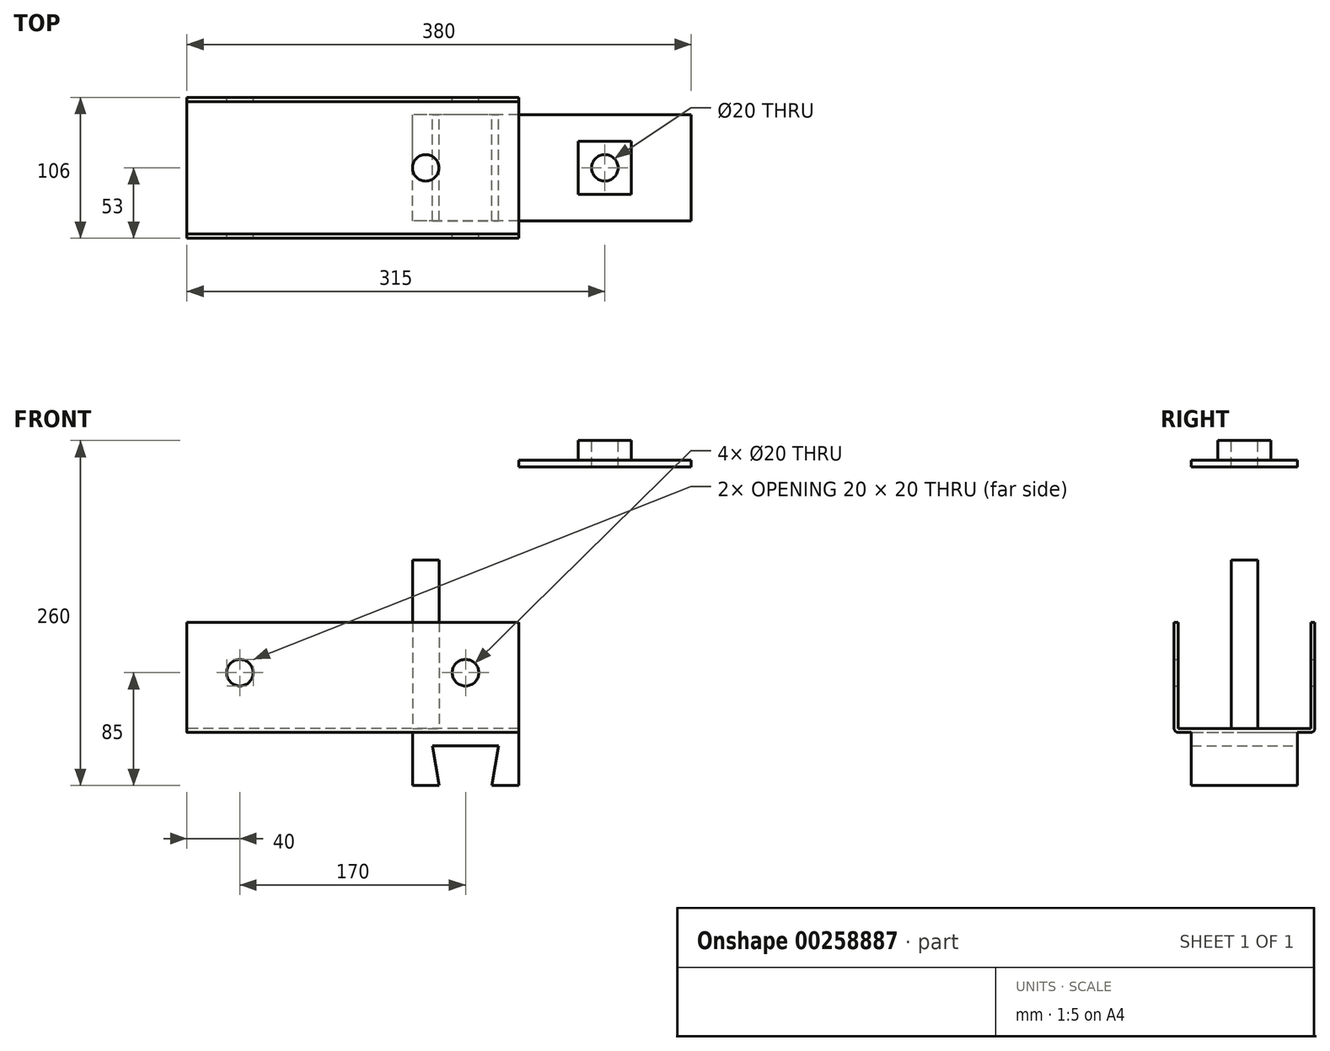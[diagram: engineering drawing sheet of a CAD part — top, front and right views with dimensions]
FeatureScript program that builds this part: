
annotation { "Feature Type Name" : "Feature", "Feature Type Description" : "" }
export const myFeature = defineFeature(function(context is Context, id is Id, definition is map)
    precondition{}
    {
        {
            var Q0;
            Q0=qCreatedBy(makeId("Front.planeOp"),FACE);
            var sketch = newSketch(context, id + "F0", { "sketchPlane" : qUnion([Q0])});
            skLineSegment(sketch, "E0", {"start": v(0, 0) * mm, "end": v(0, 5) * mm});
            skLineSegment(sketch, "E1", {"start": v(0, 5) * mm, "end": v(250, 5) * mm});
            skLineSegment(sketch, "E2", {"start": v(250, 5) * mm, "end": v(250, 0) * mm});
            skLineSegment(sketch, "E3", {"start": v(250, 0) * mm, "end": v(0, 0) * mm});
            skLineSegment(sketch, "E4", {"start": v(0, 5) * mm, "end": v(0, 85) * mm});
            skLineSegment(sketch, "E5", {"start": v(0, 85) * mm, "end": v(250, 85) * mm});
            skLineSegment(sketch, "E6", {"start": v(250, 85) * mm, "end": v(250, 5) * mm});
            skLineSegment(sketch, "E7", {"start": v(0, 45) * mm, "end": v(40, 45) * mm, "construction": true});
            skLineSegment(sketch, "E8", {"start": v(40, 45) * mm, "end": v(40, 85) * mm, "construction": true});
            skLineSegment(sketch, "E9", {"start": v(40, 5) * mm, "end": v(40, 45) * mm, "construction": true});
            skCircle(sketch, "E10", {"center": v(40, 45) * mm, "radius": 10 * mm});
            skLineSegment(sketch, "E11", {"start": v(210, 85) * mm, "end": v(210, 45) * mm, "construction": true});
            skLineSegment(sketch, "E12", {"start": v(210, 45) * mm, "end": v(250, 45) * mm, "construction": true});
            skLineSegment(sketch, "E13", {"start": v(210, 5) * mm, "end": v(210, 45) * mm, "construction": true});
            skCircle(sketch, "E14", {"center": v(210, 45) * mm, "radius": 10 * mm});
            skLineSegment(sketch, "E15", {"start": v(250, 0) * mm, "end": v(250, -40) * mm});
            skLineSegment(sketch, "E16", {"start": v(250, -40) * mm, "end": v(230, -40) * mm});
            skLineSegment(sketch, "E17", {"start": v(230, -40) * mm, "end": v(235, -10) * mm});
            skLineSegment(sketch, "E18", {"start": v(235, -10) * mm, "end": v(185, -10) * mm});
            skLineSegment(sketch, "E19", {"start": v(185, -10) * mm, "end": v(190, -40) * mm});
            skLineSegment(sketch, "E20", {"start": v(190, -40) * mm, "end": v(170, -40) * mm});
            skLineSegment(sketch, "E21", {"start": v(170, -40) * mm, "end": v(170, 0) * mm});
            skLineSegment(sketch, "E22", {"start": v(250, 200) * mm, "end": v(380, 200) * mm});
            skLineSegment(sketch, "E23", {"start": v(380, 200) * mm, "end": v(380, 205) * mm});
            skLineSegment(sketch, "E24", {"start": v(250, 205) * mm, "end": v(250, 200) * mm});
            skLineSegment(sketch, "E25", {"start": v(295, 205) * mm, "end": v(295, 220) * mm});
            skLineSegment(sketch, "E26", {"start": v(295, 220) * mm, "end": v(335, 220) * mm});
            skLineSegment(sketch, "E27", {"start": v(335, 220) * mm, "end": v(335, 205) * mm});
            skLineSegment(sketch, "E28", {"start": v(250, 205) * mm, "end": v(295, 205) * mm});
            skLineSegment(sketch, "E29", {"start": v(335, 205) * mm, "end": v(380, 205) * mm});
            skSolve(sketch);
        }
        {
            var Q0;
            Q0=qCreatedBy(makeId("Right.planeOp"),FACE);
            var sketch = newSketch(context, id + "F1", { "sketchPlane" : qUnion([Q0])});
            skLineSegment(sketch, "E30", {"start": v(0, 0) * mm, "end": v(50, 0) * mm});
            skLineSegment(sketch, "E31", {"start": v(53, 3) * mm, "end": v(53, 83) * mm});
            skLineSegment(sketch, "E32", {"start": v(53, 83) * mm, "end": v(50, 83) * mm});
            skLineSegment(sketch, "E33", {"start": v(50, 83) * mm, "end": v(50, 3) * mm});
            skLineSegment(sketch, "E34", {"start": v(50, 3) * mm, "end": v(-50, 3) * mm});
            skLineSegment(sketch, "E35", {"start": v(-50, 3) * mm, "end": v(-50, 83) * mm});
            skLineSegment(sketch, "E36", {"start": v(-50, 83) * mm, "end": v(-53, 83) * mm});
            skLineSegment(sketch, "E37", {"start": v(-53, 83) * mm, "end": v(-53, 3) * mm});
            skLineSegment(sketch, "E38", {"start": v(-50, 0) * mm, "end": v(0, 0) * mm});
            skPoint(sketch, "E39.visualSharp", {"position": v(-53, 0) * mm});
            skArc(sketch, "E39.filletArc", {"start": v(-53, 3) * mm, "mid": v(-52.12, 0.88) * mm, "end": v(-50, 0) * mm});
            skPoint(sketch, "E40.visualSharp", {"position": v(53, 0) * mm});
            skArc(sketch, "E40.filletArc", {"start": v(50, 0) * mm, "mid": v(52.12, 0.88) * mm, "end": v(53, 3) * mm});
            skLineSegment(sketch, "E41", {"start": v(-40, 0) * mm, "end": v(-40, -40) * mm});
            skLineSegment(sketch, "E42", {"start": v(-40, -40) * mm, "end": v(0, -40) * mm});
            skLineSegment(sketch, "E43", {"start": v(0, -40) * mm, "end": v(40, -40) * mm});
            skLineSegment(sketch, "E44", {"start": v(40, -40) * mm, "end": v(40, 0) * mm});
            skLineSegment(sketch, "E45", {"start": v(0, 200) * mm, "end": v(40, 200) * mm});
            skLineSegment(sketch, "E46", {"start": v(40, 200) * mm, "end": v(40, 205) * mm});
            skLineSegment(sketch, "E47", {"start": v(40, 205) * mm, "end": v(20, 205) * mm});
            skLineSegment(sketch, "E48", {"start": v(20, 205) * mm, "end": v(20, 220) * mm});
            skLineSegment(sketch, "E49", {"start": v(20, 220) * mm, "end": v(-20, 220) * mm});
            skLineSegment(sketch, "E50", {"start": v(-20, 220) * mm, "end": v(-20, 205) * mm});
            skLineSegment(sketch, "E51", {"start": v(-20, 205) * mm, "end": v(-40, 205) * mm});
            skLineSegment(sketch, "E52", {"start": v(-40, 205) * mm, "end": v(-40, 200) * mm});
            skLineSegment(sketch, "E53", {"start": v(-40, 200) * mm, "end": v(0, 200) * mm});
            skSolve(sketch);
        }
        {
            var Q0;
            Q0=qCreatedBy(makeId("Top.planeOp"),FACE);
            var sketch = newSketch(context, id + "F2", { "sketchPlane" : qUnion([Q0])});
            skCircle(sketch, "E54", {"center": v(180, 0) * mm, "radius": 10 * mm});
            skSolve(sketch);
        }
        {
            var Q0;
            Q0=makeQuery(id+"F0.imprint","IMPRINT",FACE,{"disambiguationData":[TD([[makeQuery(id+"F0.imprint","IMPRINT",EDGE,{"derivedFrom":sQuery(id+"F0.wireOp",EDGE,"E1")}),1.0]])]});
            var Q1;
            {var subQ3=sQuery(id+"F0.wireOp",EDGE,"E0");Q1=makeQuery(id+"F0.imprint","IMPRINT",FACE,{"disambiguationData":[TD([[makeQuery(id+"F0.imprint","IMPRINT",EDGE,{"derivedFrom":subQ3}),-1.0]])]});}
            var Q2;
            {var subQ0=sQuery(id+"F0.wireOp",EDGE,"E15");Q2=makeQuery(id+"F0.imprint","IMPRINT",FACE,{"disambiguationData":[TD([[makeQuery(id+"F0.imprint","IMPRINT",EDGE,{"derivedFrom":subQ0}),-1.0]])]});}
            var Q3;
            Q3=makeQuery(id+"F0.imprint","IMPRINT",FACE,{"disambiguationData":[TD([[makeQuery(id+"F0.imprint","IMPRINT",EDGE,{"derivedFrom":sQuery(id+"F0.wireOp",EDGE,"E22")}),1.0]])]});
            extrude(context, id + "F3", {"entities" : qUnion([Q0, Q1, Q2, Q3]), "depth" : 206 * mm, "symmetric" : true});
        }
        {
            var Q0;
            Q0 = qSketchRegion(id + "F1", true);
            extrude(context, id + "F4", {"entities" : qUnion([Q0]), "operationType" : NewBodyOperationType.INTERSECT, "depth" : 437 * mm});
        }
        {
            var Q0;
            Q0 = qSketchRegion(id + "F2", true);
            extrude(context, id + "F5", {"entities" : qUnion([Q0]), "operationType" : NewBodyOperationType.ADD, "depth" : 130 * mm});
        }
        {
            var Q0;
            Q0=makeQuery(id+"F3.opExtrude","SWEPT_FACE",FACE,{"disambiguationData":[OSD([sQuery(id+"F0.wireOp",EDGE,"E26")])]});
            var sketch = newSketch(context, id + "F6", { "sketchPlane" : qUnion([Q0])});
            skLineSegment(sketch, "E55.0.0", {"start": v(335, -20) * mm, "end": v(335, 20) * mm});
            skLineSegment(sketch, "E55.0.1", {"start": v(335, 20) * mm, "end": v(295, 20) * mm});
            skLineSegment(sketch, "E55.0.2", {"start": v(295, 20) * mm, "end": v(295, -20) * mm});
            skLineSegment(sketch, "E55.0.3", {"start": v(295, -20) * mm, "end": v(335, -20) * mm});
            skLineSegment(sketch, "E56", {"start": v(295, -20) * mm, "end": v(335, 20) * mm});
            skPoint(sketch, "E57", {"position": v(315, 0) * mm});
            skSolve(sketch);
        }
        {
            var Q0;
            Q0=sQuery(id+"F6.wireOp",VERTEX,"E57");
            var Q1;
            Q1=makeQuery(id+"F3.opExtrude","SWEPT_BODY",BODY,{"disambiguationData":[OSD([sQuery(id+"F0.wireOp",EDGE,"E22"),sQuery(id+"F0.wireOp",EDGE,"E23"),sQuery(id+"F0.wireOp",EDGE,"E24"),sQuery(id+"F0.wireOp",EDGE,"E25"),sQuery(id+"F0.wireOp",EDGE,"E26"),sQuery(id+"F0.wireOp",EDGE,"E27"),sQuery(id+"F0.wireOp",EDGE,"E28"),sQuery(id+"F0.wireOp",EDGE,"E29")])]});
            hole(context, id + "F7", {"style" : HoleStyle.SIMPLE, "endStyle" : HoleEndStyle.THROUGH, "holeDiameter" : 20 * mm, "tappedDepth" : 12 * mm, "tapClearance" : 3, "locations" : qUnion([Q0]), "scope" : qUnion([Q1])});
        }
    });
